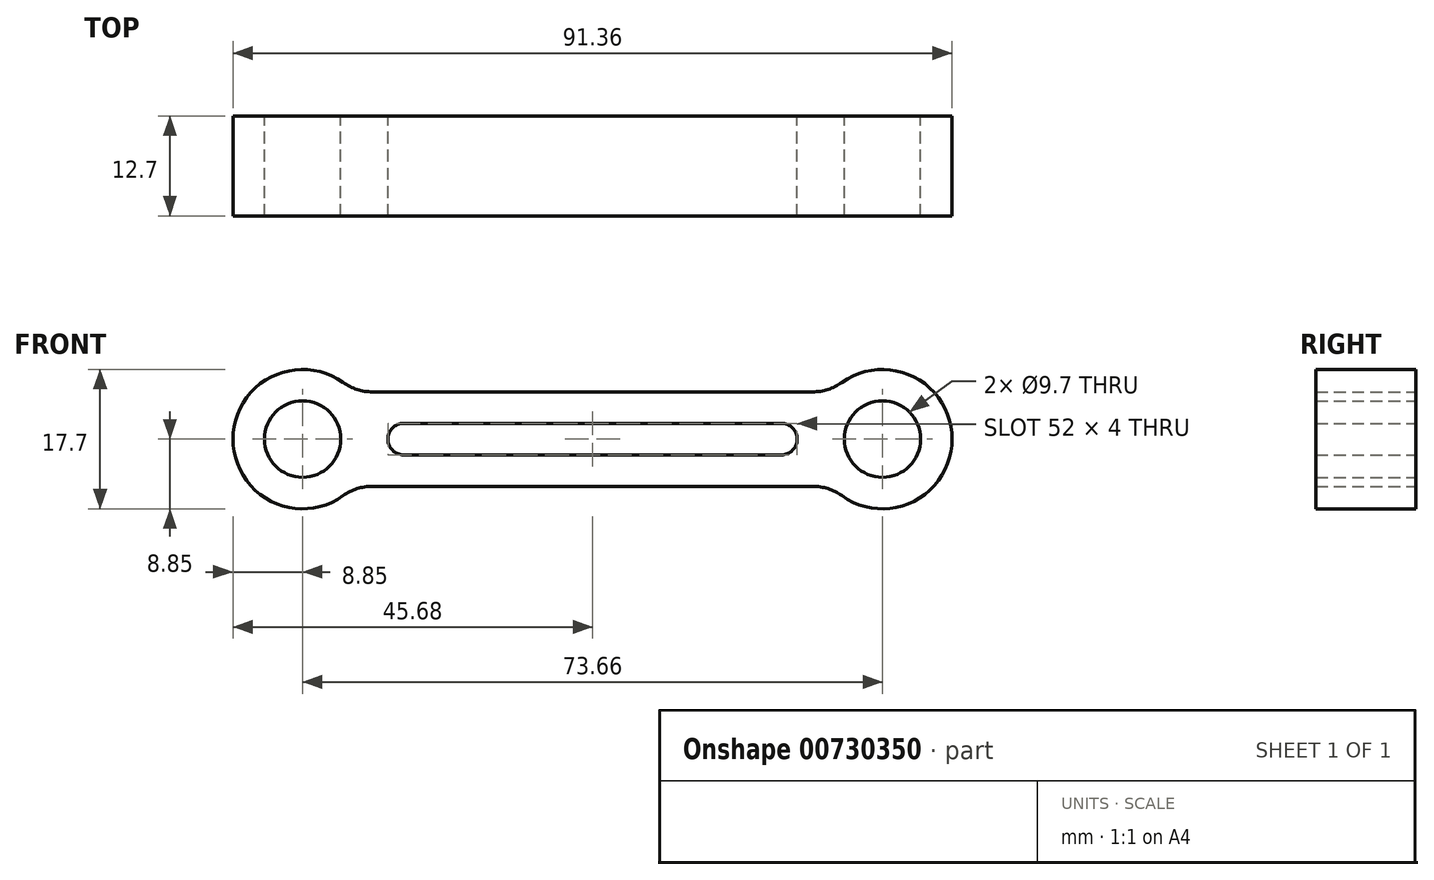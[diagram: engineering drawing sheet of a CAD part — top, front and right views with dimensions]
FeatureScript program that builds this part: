
annotation { "Feature Type Name" : "Feature", "Feature Type Description" : "" }
export const myFeature = defineFeature(function(context is Context, id is Id, definition is map)
    precondition{}
    {
        {
            var Q0;
            Q0=qCreatedBy(makeId("Front.planeOp"),FACE);
            var sketch = newSketch(context, id + "F0", { "sketchPlane" : qUnion([Q0])});
            skCircle(sketch, "E0", {"center": v(-36.83, 0) * mm, "radius": 4.45 * mm});
            skCircle(sketch, "E1", {"center": v(36.83, 0) * mm, "radius": 4.45 * mm});
            skLineSegment(sketch, "E2", {"start": v(-36.83, 0) * mm, "end": v(36.83, 0) * mm, "construction": true});
            skSolve(sketch);
        }
        {
            var Q0;
            Q0=qCreatedBy(makeId("Front.planeOp"),FACE);
            var sketch = newSketch(context, id + "F1", { "sketchPlane" : qUnion([Q0])});
            skCircle(sketch, "E3.0", {"center": v(-36.83, 0) * mm, "radius": 4.45 * mm, "construction": true});
            skCircle(sketch, "E4.0", {"center": v(36.83, 0) * mm, "radius": 4.45 * mm, "construction": true});
            skCircle(sketch, "E5.0", {"center": v(-36.83, 0) * mm, "radius": 4.85 * mm});
            skCircle(sketch, "E6", {"center": v(36.83, 0) * mm, "radius": 4.85 * mm});
            skArc(sketch, "E7.0", {"start": v(-31.67, 7.2) * mm, "mid": v(-45.68, 0) * mm, "end": v(-31.67, -7.2) * mm});
            skArc(sketch, "E8", {"start": v(31.67, -7.2) * mm, "mid": v(45.68, 0) * mm, "end": v(31.67, 7.2) * mm});
            skLineSegment(sketch, "E9", {"start": v(-27.97, 6) * mm, "end": v(27.97, 6) * mm});
            skLineSegment(sketch, "E10", {"start": v(27.97, -6) * mm, "end": v(-27.97, -6) * mm});
            skPoint(sketch, "E11.visualSharp", {"position": v(-30.32, 6) * mm});
            skArc(sketch, "E11.filletArc", {"start": v(-31.67, 7.2) * mm, "mid": v(-29.91, 6.3) * mm, "end": v(-27.97, 6) * mm});
            skPoint(sketch, "E12.visualSharp", {"position": v(-30.32, -6) * mm});
            skArc(sketch, "E12.filletArc", {"start": v(-27.97, -6) * mm, "mid": v(-29.91, -6.3) * mm, "end": v(-31.67, -7.2) * mm});
            skPoint(sketch, "E13.visualSharp", {"position": v(30.32, -6) * mm});
            skArc(sketch, "E13.filletArc", {"start": v(31.67, -7.2) * mm, "mid": v(29.91, -6.3) * mm, "end": v(27.97, -6) * mm});
            skPoint(sketch, "E14.visualSharp", {"position": v(30.32, 6) * mm});
            skArc(sketch, "E14.filletArc", {"start": v(27.97, 6) * mm, "mid": v(29.91, 6.3) * mm, "end": v(31.67, 7.2) * mm});
            skLineSegment(sketch, "E15", {"start": v(0, -6) * mm, "end": v(0, 6) * mm, "construction": true});
            skSolve(sketch);
        }
        {
            var Q0;
            Q0 = qSketchRegion(id + "F1", true);
            extrude(context, id + "F2", {"entities" : qUnion([Q0]), "depth" : 12.7 * mm, "offsetDistance" : 25.4 * mm});
        }
        {
            var Q0;
            Q0=qCreatedBy(makeId("Front.planeOp"),FACE);
            var sketch = newSketch(context, id + "F3", { "sketchPlane" : qUnion([Q0])});
            skLineSegment(sketch, "E16", {"start": v(-24, 0) * mm, "end": v(24, 0) * mm});
            skArc(sketch, "E17.0.startCap", {"start": v(-24, -2) * mm, "mid": v(-26, 0) * mm, "end": v(-24, 2) * mm});
            skArc(sketch, "E17.0.endCap", {"start": v(24, 2) * mm, "mid": v(26, 0) * mm, "end": v(24, -2) * mm});
            skLineSegment(sketch, "E17.0.left", {"start": v(-24, 2) * mm, "end": v(24, 2) * mm});
            skLineSegment(sketch, "E17.0.right", {"start": v(-24, -2) * mm, "end": v(24, -2) * mm});
            skSolve(sketch);
        }
        {
            var Q0;
            Q0 = qSketchRegion(id + "F3", true);
            extrude(context, id + "F4", {"entities" : qUnion([Q0]), "operationType" : NewBodyOperationType.REMOVE, "endBound" : BoundingType.THROUGH_ALL, "depth" : 25.4 * mm, "offsetDistance" : 25.4 * mm});
        }
    });
